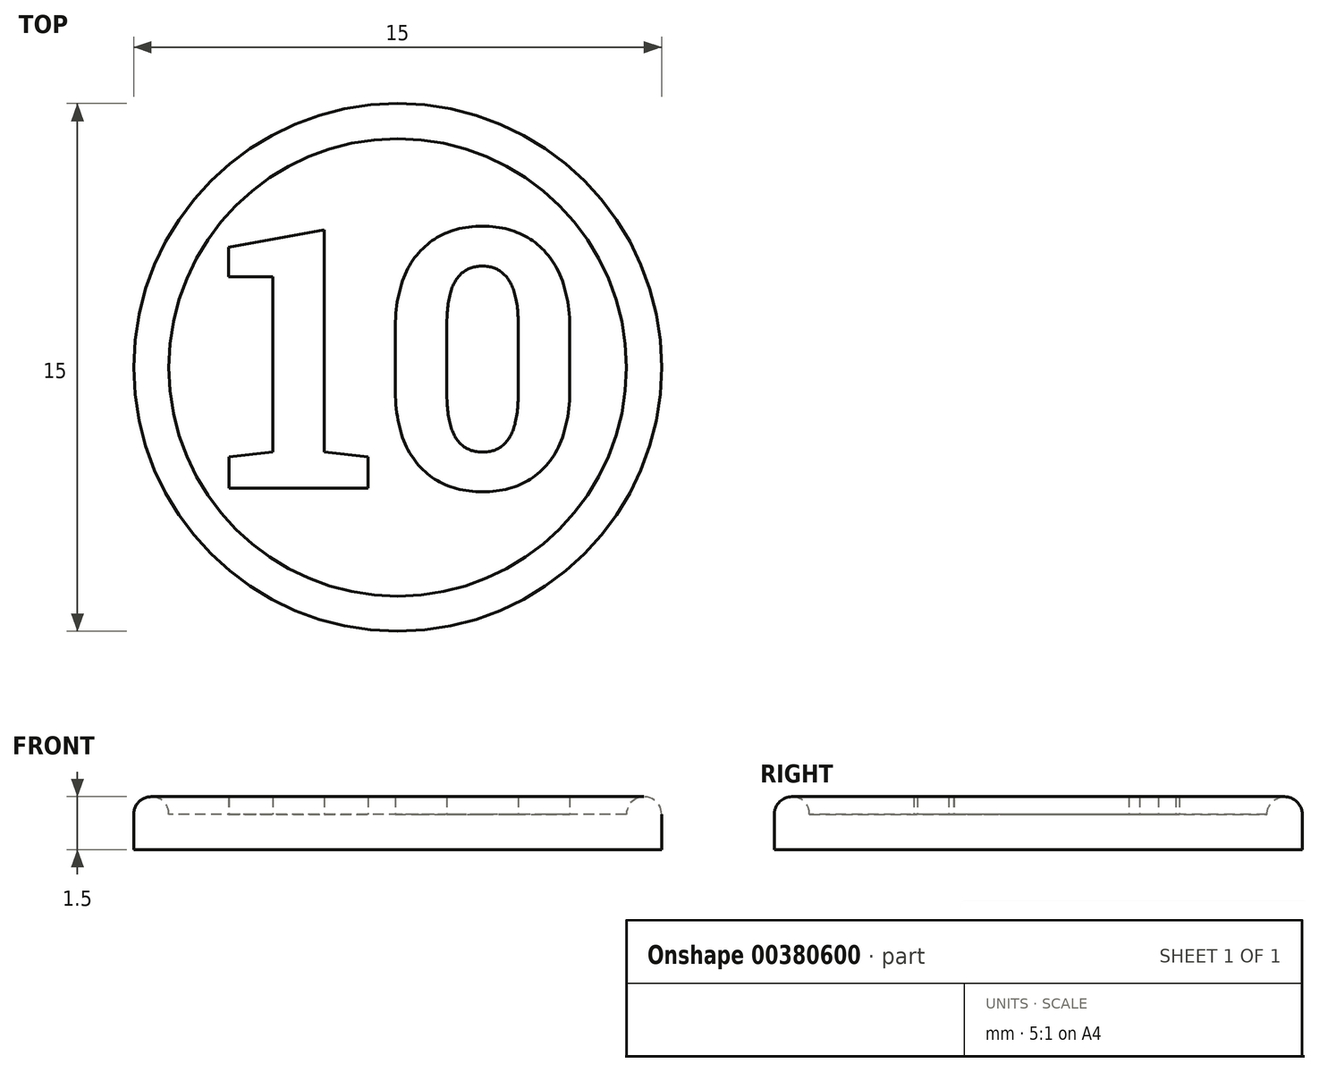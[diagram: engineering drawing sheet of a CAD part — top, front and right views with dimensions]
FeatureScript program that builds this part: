
annotation { "Feature Type Name" : "Feature", "Feature Type Description" : "" }
export const myFeature = defineFeature(function(context is Context, id is Id, definition is map)
    precondition{}
    {
        {
            var Q0;
            Q0=qCreatedBy(makeId("Top.planeOp"),FACE);
            var sketch = newSketch(context, id + "F0", { "sketchPlane" : qUnion([Q0])});
            skCircle(sketch, "E0", {"center": v(0, 0) * mm, "radius": 7.5 * mm});
            skCircle(sketch, "E1", {"center": v(0, 0) * mm, "radius": 6.5 * mm});
            skSolve(sketch);
        }
        {
            var Q0;
            Q0=makeQuery(id+"F0.imprint","IMPRINT",FACE,{"disambiguationData":[TD([[makeQuery(id+"F0.imprint","IMPRINT",EDGE,{"derivedFrom":sQuery(id+"F0.wireOp",EDGE,"E0")}),1.0]])]});
            extrude(context, id + "F1", {"entities" : qUnion([Q0]), "depth" : 1.5 * mm});
        }
        {
            var Q0;
            Q0=makeQuery(id+"F0.imprint","IMPRINT",FACE,{"disambiguationData":[TD([[makeQuery(id+"F0.imprint","IMPRINT",EDGE,{"derivedFrom":sQuery(id+"F0.wireOp",EDGE,"E1")}),1.0]])]});
            extrude(context, id + "F2", {"entities" : qUnion([Q0]), "operationType" : NewBodyOperationType.ADD, "depth" : 1 * mm});
        }
        {
            var Q0;
            Q0=makeQuery(id+"F1.opExtrude","CAP_EDGE",EDGE,{"disambiguationData":[OSD([sQuery(id+"F0.wireOp",EDGE,"E0")])],"isStart":false});
            fillet(context, id + "F3", {"entities" : qUnion([Q0]), "radius" : 0.5 * mm, "tangentPropagation" : true, "allowEdgeOverflow" : false});
        }
        {
            var Q0;
            Q0=makeQuery(id+"F1.opExtrude","CAP_EDGE",EDGE,{"disambiguationData":[OSD([sQuery(id+"F0.wireOp",EDGE,"E1")])],"isStart":false});
            fillet(context, id + "F4", {"entities" : qUnion([Q0]), "radius" : 0.5 * mm, "tangentPropagation" : true, "allowEdgeOverflow" : false});
        }
        {
            var Q0;
            Q0=makeQuery(id+"F2.opExtrude","CAP_FACE",FACE,{"disambiguationData":[OSD([sQuery(id+"F0.wireOp",EDGE,"E1")])],"isStart":false});
            var sketch = newSketch(context, id + "F5", { "sketchPlane" : qUnion([Q0])});
            skText(sketch, "E2", { "text": "10", "fontName": "RobotoSlab-Bold.ttf"});
            const initialGuessF5  = {"E2": [-0.00512, -0.00343, 1, 0, 0.00743]};
            skSetInitialGuess(sketch, initialGuessF5);
            skSolve(sketch);
        }
        {
            var Q0;
            Q0 = qSketchRegion(id + "F5", true);
            extrude(context, id + "F6", {"entities" : qUnion([Q0]), "operationType" : NewBodyOperationType.ADD, "depth" : 0.5 * mm});
        }
    });
